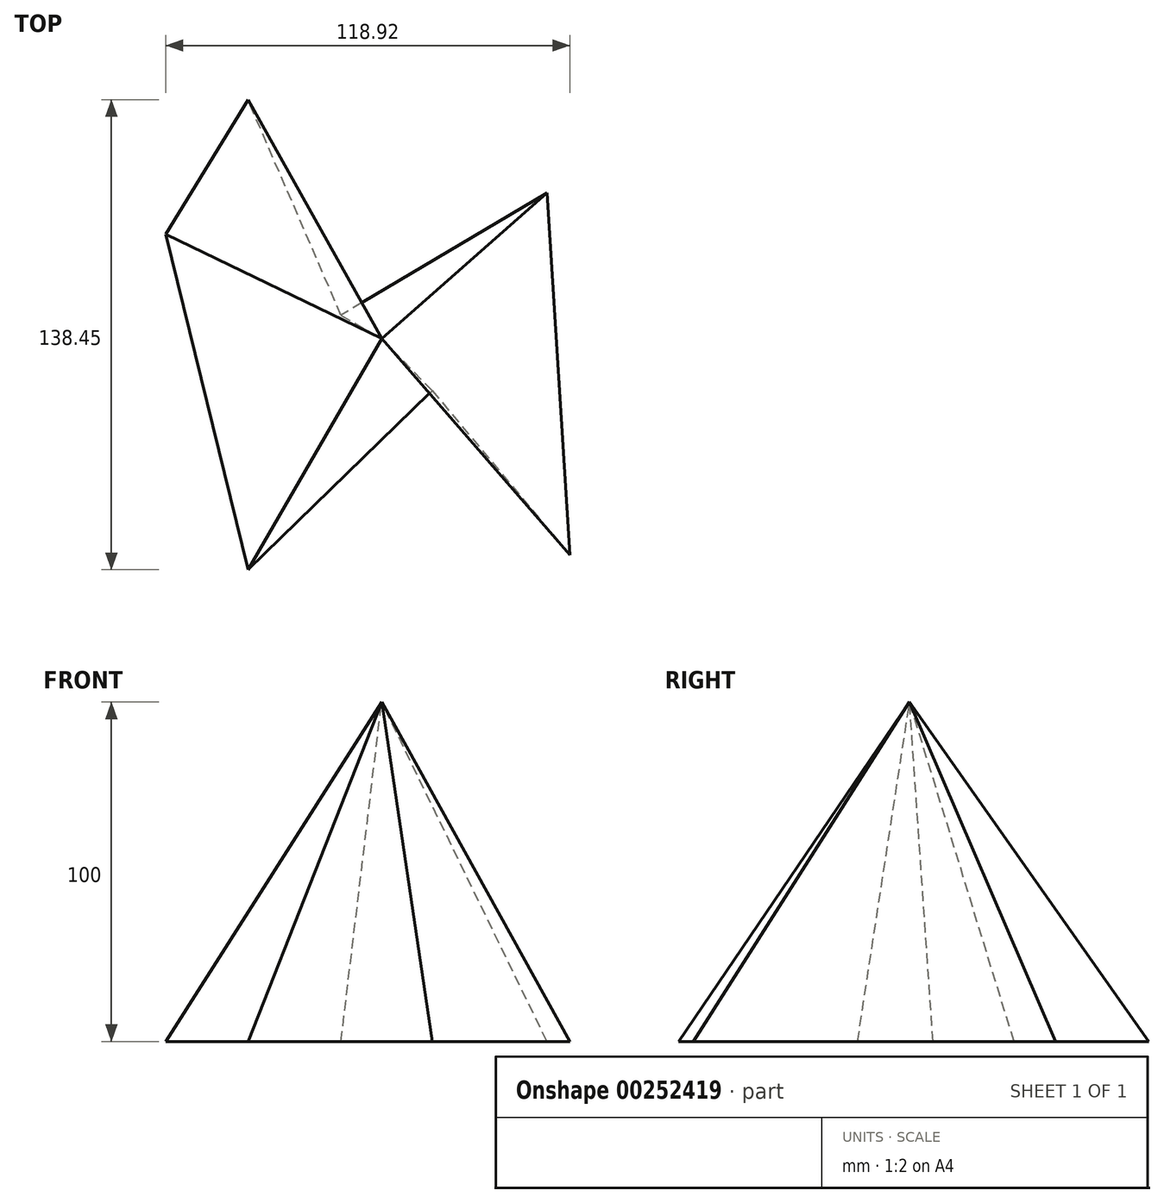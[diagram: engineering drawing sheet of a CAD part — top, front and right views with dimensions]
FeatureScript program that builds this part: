
annotation { "Feature Type Name" : "Feature", "Feature Type Description" : "" }
export const myFeature = defineFeature(function(context is Context, id is Id, definition is map)
    precondition{}
    {
        {
            var Q0;
            Q0=qCreatedBy(makeId("Top.planeOp"),FACE);
            var sketch = newSketch(context, id + "F0", { "sketchPlane" : qUnion([Q0])});
            skLineSegment(sketch, "E0", {"start": v(-63.54, 30.75) * mm, "end": v(-39.35, -68.06) * mm});
            skLineSegment(sketch, "E1", {"start": v(-39.35, -68.06) * mm, "end": v(14.87, -15.3) * mm});
            skLineSegment(sketch, "E2", {"start": v(14.87, -15.3) * mm, "end": v(55.38, -63.69) * mm});
            skLineSegment(sketch, "E3", {"start": v(55.38, -63.69) * mm, "end": v(48.68, 43) * mm});
            skLineSegment(sketch, "E4", {"start": v(48.68, 43) * mm, "end": v(-12.53, 6.56) * mm});
            skLineSegment(sketch, "E5", {"start": v(-11.95, 6.85) * mm, "end": v(-39.35, 70.4) * mm});
            skLineSegment(sketch, "E6", {"start": v(-63.54, 30.75) * mm, "end": v(-39.35, 70.4) * mm});
            skSolve(sketch);
        }
        {
            var Q0;
            Q0=qCreatedBy(makeId("Top.planeOp"),FACE);
            cPlane(context, id + "F1", {"entities" : qUnion([Q0]), "cplaneType" : CPlaneType.OFFSET, "offset" : 100 * mm, "width" : 152.4 * mm, "height" : 152.4 * mm});
        }
        {
            var Q0;
            Q0=qCreatedBy(id+"F1.planeOp",FACE);
            var sketch = newSketch(context, id + "F2", { "sketchPlane" : qUnion([Q0])});
            skPoint(sketch, "E7", {"position": v(0, 0) * mm});
            skSolve(sketch);
        }
        {
            var Q0;
            Q0=makeQuery(id+"F0.imprint","IMPRINT",FACE,{"disambiguationData":[TD([[makeQuery(id+"F0.imprint","IMPRINT",EDGE,{"derivedFrom":sQuery(id+"F0.wireOp",EDGE,"E0")}),1.0]])]});
            var Q1;
            Q1=sQuery(id+"F2.wireOp",VERTEX,"E7");
            loft(context, id + "F3", {"sheetProfilesArray" : [{ "sheetProfileEntities" : qUnion([Q0]) }, { "sheetProfileEntities" : qUnion([Q1]) }]});
        }
    });
